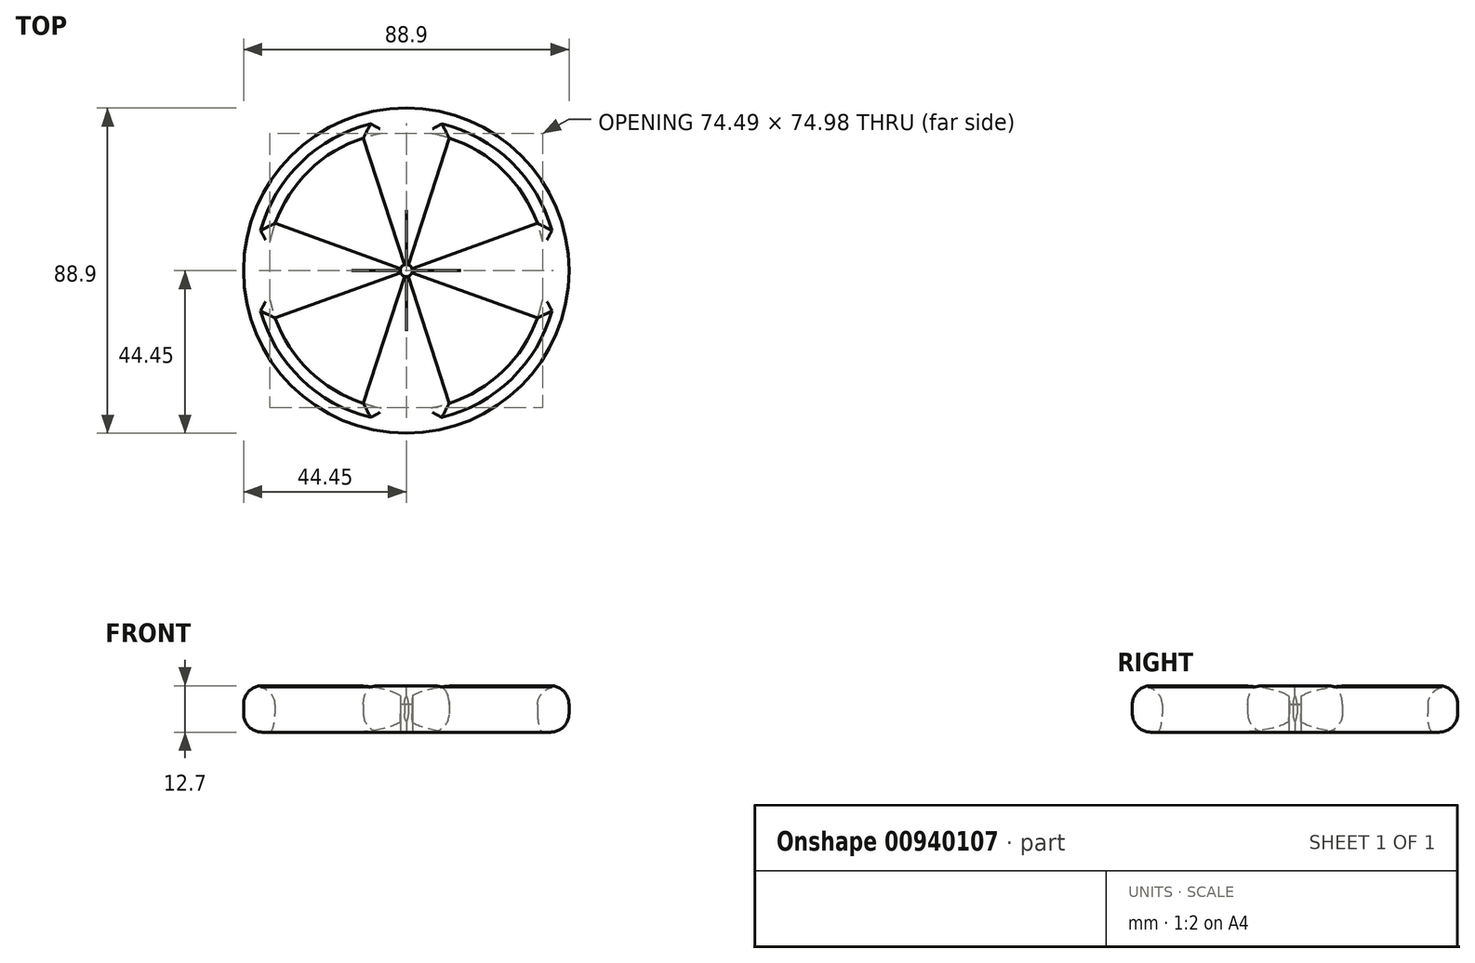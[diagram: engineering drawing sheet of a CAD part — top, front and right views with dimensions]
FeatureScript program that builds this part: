
annotation { "Feature Type Name" : "Feature", "Feature Type Description" : "" }
export const myFeature = defineFeature(function(context is Context, id is Id, definition is map)
    precondition{}
    {
        {
            var Q0;
            Q0=qCreatedBy(makeId("Top.planeOp"),FACE);
            var sketch = newSketch(context, id + "F0", { "sketchPlane" : qUnion([Q0])});
            skCircle(sketch, "E0", {"center": v(0, 0) * mm, "radius": 38.1 * mm});
            skLineSegment(sketch, "E1", {"start": v(0, 0) * mm, "end": v(-38.1, 0) * mm});
            skLineSegment(sketch, "E2", {"start": v(-38.1, 0) * mm, "end": v(38.1, 0) * mm});
            skLineSegment(sketch, "E3", {"start": v(0, 38.1) * mm, "end": v(0, -38.1) * mm});
            skLineSegment(sketch, "E4", {"start": v(0, 0) * mm, "end": v(-35.84, 12.92) * mm});
            skLineSegment(sketch, "E5.MirrorCS", {"start": v(0, 0) * mm, "end": v(35.84, 12.92) * mm});
            skLineSegment(sketch, "E6.MirrorCS", {"start": v(0, 0) * mm, "end": v(-35.84, -12.92) * mm});
            skLineSegment(sketch, "E7.MirrorCS", {"start": v(0, 0) * mm, "end": v(35.84, -12.92) * mm});
            skLineSegment(sketch, "E8", {"start": v(0, 0) * mm, "end": v(11.73, -36.25) * mm});
            skLineSegment(sketch, "E9.MirrorCS", {"start": v(0, 0) * mm, "end": v(-11.73, -36.25) * mm});
            skCircle(sketch, "E10.0", {"center": v(0, 0) * mm, "radius": 44.45 * mm});
            skCircle(sketch, "E11", {"center": v(0, 0) * mm, "radius": 1.66 * mm});
            skLineSegment(sketch, "E12.MirrorCS", {"start": v(0, 0) * mm, "end": v(11.73, 36.25) * mm});
            skLineSegment(sketch, "E13.MirrorCS", {"start": v(0, 0) * mm, "end": v(-11.73, 36.25) * mm});
            skSolve(sketch);
        }
        {
            var Q0;
            Q0=makeQuery(id+"F0.imprint","IMPRINT",FACE,{"disambiguationData":[TD([[makeQuery(id+"F0.imprint","IMPRINT",EDGE,{"derivedFrom":sQuery(id+"F0.wireOp",EDGE,"E10.0")}),1.0]])]});
            var Q1;
            {var subQ0=sQuery(id+"F0.wireOp",EDGE,"E3");var subQ1=sQuery(id+"F0.wireOp",EDGE,"E0");var subQ2=makeQuery(id+"F0.imprint","INTERSECT",VERTEX,{"disambiguationData":[OD(1.0)],"derivedFrom":[subQ1,subQ0]});Q1=makeQuery(id+"F0.imprint","IMPRINT",FACE,{"disambiguationData":[TD([[makeQuery(id+"F0.imprint","IMPRINT",EDGE,{"disambiguationData":[TD([[subQ2,-1.0]])],"derivedFrom":subQ1}),1.0]])]});}
            var Q2;
            {var subQ0=sQuery(id+"F0.wireOp",EDGE,"E9.MirrorCS");var subQ1=sQuery(id+"F0.wireOp",EDGE,"E0");var subQ2=makeQuery(id+"F0.imprint","INTERSECT",VERTEX,{"derivedFrom":[subQ1,subQ0]});Q2=makeQuery(id+"F0.imprint","IMPRINT",FACE,{"disambiguationData":[TD([[makeQuery(id+"F0.imprint","IMPRINT",EDGE,{"disambiguationData":[TD([[subQ2,-1.0]])],"derivedFrom":subQ1}),1.0]])]});}
            var Q3;
            {var subQ0=sQuery(id+"F0.wireOp",EDGE,"E4");var subQ1=sQuery(id+"F0.wireOp",EDGE,"E0");var subQ2=makeQuery(id+"F0.imprint","INTERSECT",VERTEX,{"derivedFrom":[subQ1,subQ0]});Q3=makeQuery(id+"F0.imprint","IMPRINT",FACE,{"disambiguationData":[TD([[makeQuery(id+"F0.imprint","IMPRINT",EDGE,{"disambiguationData":[TD([[subQ2,-1.0]])],"derivedFrom":subQ1}),1.0]])]});}
            var Q4;
            {var subQ0=sQuery(id+"F0.wireOp",EDGE,"E1");var subQ1=sQuery(id+"F0.wireOp",EDGE,"E0");var subQ2=makeQuery(id+"F0.imprint","INTERSECT",VERTEX,{"derivedFrom":[subQ1,subQ0]});Q4=makeQuery(id+"F0.imprint","IMPRINT",FACE,{"disambiguationData":[TD([[makeQuery(id+"F0.imprint","IMPRINT",EDGE,{"disambiguationData":[TD([[subQ2,-1.0]])],"derivedFrom":subQ1}),1.0]])]});}
            var Q5;
            {var subQ0=sQuery(id+"F0.wireOp",EDGE,"E5.MirrorCS");var subQ1=sQuery(id+"F0.wireOp",EDGE,"E0");var subQ2=makeQuery(id+"F0.imprint","INTERSECT",VERTEX,{"derivedFrom":[subQ1,subQ0]});Q5=makeQuery(id+"F0.imprint","IMPRINT",FACE,{"disambiguationData":[TD([[makeQuery(id+"F0.imprint","IMPRINT",EDGE,{"disambiguationData":[TD([[subQ2,1.0]])],"derivedFrom":subQ1}),1.0]])]});}
            var Q6;
            {var subQ0=sQuery(id+"F0.wireOp",EDGE,"E2");var subQ1=sQuery(id+"F0.wireOp",EDGE,"E0");var subQ2=makeQuery(id+"F0.imprint","INTERSECT",VERTEX,{"derivedFrom":[subQ1,subQ0]});Q6=makeQuery(id+"F0.imprint","IMPRINT",FACE,{"disambiguationData":[TD([[makeQuery(id+"F0.imprint","IMPRINT",EDGE,{"disambiguationData":[TD([[subQ2,1.0]])],"derivedFrom":subQ1}),1.0]])]});}
            var Q7;
            {var subQ0=sQuery(id+"F0.wireOp",EDGE,"E3");var subQ1=sQuery(id+"F0.wireOp",EDGE,"E0");var subQ2=makeQuery(id+"F0.imprint","INTERSECT",VERTEX,{"disambiguationData":[OD(0.0)],"derivedFrom":[subQ1,subQ0]});Q7=makeQuery(id+"F0.imprint","IMPRINT",FACE,{"disambiguationData":[TD([[makeQuery(id+"F0.imprint","IMPRINT",EDGE,{"disambiguationData":[TD([[subQ2,-1.0]])],"derivedFrom":subQ1}),1.0]])]});}
            var Q8;
            {var subQ0=sQuery(id+"F0.wireOp",EDGE,"E3");var subQ1=sQuery(id+"F0.wireOp",EDGE,"E0");var subQ2=makeQuery(id+"F0.imprint","INTERSECT",VERTEX,{"disambiguationData":[OD(0.0)],"derivedFrom":[subQ1,subQ0]});Q8=makeQuery(id+"F0.imprint","IMPRINT",FACE,{"disambiguationData":[TD([[makeQuery(id+"F0.imprint","IMPRINT",EDGE,{"disambiguationData":[TD([[subQ2,1.0]])],"derivedFrom":subQ1}),1.0]])]});}
            extrude(context, id + "F1", {"entities" : qUnion([Q0, Q1, Q2, Q3, Q4, Q5, Q6, Q7, Q8]), "depth" : 12.7 * mm, "offsetDistance" : 25.4 * mm});
        }
        {
            var Q0;
            Q0=makeQuery(id+"F1.opExtrude","CAP_EDGE",EDGE,{"disambiguationData":[OSD([sQuery(id+"F0.wireOp",EDGE,"E10.0")])],"isStart":false});
            var Q1;
            Q1=makeQuery(id+"F1.opExtrude","CAP_EDGE",EDGE,{"disambiguationData":[OSD([sQuery(id+"F0.wireOp",EDGE,"E10.0")])],"isStart":true});
            fillet(context, id + "F2", {"entities" : qUnion([Q0, Q1]), "radius" : 5.08 * mm, "tangentPropagation" : true, "allowEdgeOverflow" : false});
        }
        {
            var Q0;
            Q0=makeQuery(id+"F1.opExtrude","CAP_EDGE",EDGE,{"disambiguationData":[OSD([sQuery(id+"F0.wireOp",EDGE,"E6.MirrorCS")])],"isStart":false});
            var Q1;
            Q1=makeQuery(id+"F1.opExtrude","CAP_EDGE",EDGE,{"disambiguationData":[OSD([sQuery(id+"F0.wireOp",EDGE,"E4")])],"isStart":false});
            var Q2;
            Q2=makeQuery(id+"F1.opExtrude","CAP_EDGE",EDGE,{"disambiguationData":[OSD([sQuery(id+"F0.wireOp",EDGE,"E6.MirrorCS")])],"isStart":true});
            var Q3;
            Q3=makeQuery(id+"F1.opExtrude","CAP_EDGE",EDGE,{"disambiguationData":[OSD([sQuery(id+"F0.wireOp",EDGE,"E8")])],"isStart":false});
            var Q4;
            Q4=makeQuery(id+"F1.opExtrude","CAP_EDGE",EDGE,{"disambiguationData":[OSD([sQuery(id+"F0.wireOp",EDGE,"E9.MirrorCS")])],"isStart":false});
            var Q5;
            Q5=makeQuery(id+"F1.opExtrude","CAP_EDGE",EDGE,{"disambiguationData":[OSD([sQuery(id+"F0.wireOp",EDGE,"E7.MirrorCS")])],"isStart":false});
            var Q6;
            Q6=makeQuery(id+"F1.opExtrude","CAP_EDGE",EDGE,{"disambiguationData":[OSD([sQuery(id+"F0.wireOp",EDGE,"E7.MirrorCS")])],"isStart":true});
            var Q7;
            Q7=makeQuery(id+"F1.opExtrude","CAP_EDGE",EDGE,{"disambiguationData":[OSD([sQuery(id+"F0.wireOp",EDGE,"E9.MirrorCS")])],"isStart":true});
            var Q8;
            Q8=makeQuery(id+"F1.opExtrude","CAP_EDGE",EDGE,{"disambiguationData":[OSD([sQuery(id+"F0.wireOp",EDGE,"E8")])],"isStart":true});
            var Q9;
            Q9=makeQuery(id+"F1.opExtrude","CAP_EDGE",EDGE,{"disambiguationData":[OSD([sQuery(id+"F0.wireOp",EDGE,"E5.MirrorCS")])],"isStart":true});
            var Q10;
            Q10=makeQuery(id+"F1.opExtrude","CAP_EDGE",EDGE,{"disambiguationData":[OSD([sQuery(id+"F0.wireOp",EDGE,"E5.MirrorCS")])],"isStart":false});
            var Q11;
            Q11=makeQuery(id+"F1.opExtrude","CAP_EDGE",EDGE,{"disambiguationData":[OSD([sQuery(id+"F0.wireOp",EDGE,"E4")])],"isStart":true});
            fillet(context, id + "F3", {"entities" : qUnion([Q0, Q1, Q2, Q3, Q4, Q5, Q6, Q7, Q8, Q9, Q10, Q11]), "radius" : 5.08 * mm, "tangentPropagation" : true, "allowEdgeOverflow" : false});
        }
        {
            var Q0;
            {var subQ0=sQuery(id+"F0.wireOp",EDGE,"E11");var subQ1=sQuery(id+"F0.wireOp",EDGE,"E1");var subQ2=makeQuery(id+"F0.imprint","INTERSECT",VERTEX,{"derivedFrom":[subQ1,subQ0]});Q0=makeQuery(id+"F0.imprint","IMPRINT",FACE,{"disambiguationData":[TD([[makeQuery(id+"F0.imprint","IMPRINT",EDGE,{"disambiguationData":[TD([[subQ2,-1.0]])],"derivedFrom":subQ0}),1.0]])]});}
            var Q1;
            {var subQ0=sQuery(id+"F0.wireOp",EDGE,"E11");var subQ1=sQuery(id+"F0.wireOp",EDGE,"E1");var subQ2=makeQuery(id+"F0.imprint","INTERSECT",VERTEX,{"derivedFrom":[subQ1,subQ0]});Q1=makeQuery(id+"F0.imprint","IMPRINT",FACE,{"disambiguationData":[TD([[makeQuery(id+"F0.imprint","IMPRINT",EDGE,{"disambiguationData":[TD([[subQ2,1.0]])],"derivedFrom":subQ0}),1.0]])]});}
            var Q2;
            {var subQ0=sQuery(id+"F0.wireOp",EDGE,"E11");var subQ1=sQuery(id+"F0.wireOp",EDGE,"E2");var subQ2=makeQuery(id+"F0.imprint","INTERSECT",VERTEX,{"derivedFrom":[subQ1,subQ0]});Q2=makeQuery(id+"F0.imprint","IMPRINT",FACE,{"disambiguationData":[TD([[makeQuery(id+"F0.imprint","IMPRINT",EDGE,{"disambiguationData":[TD([[subQ2,-1.0]])],"derivedFrom":subQ0}),1.0]])]});}
            var Q3;
            {var subQ0=sQuery(id+"F0.wireOp",EDGE,"E11");var subQ1=sQuery(id+"F0.wireOp",EDGE,"E2");var subQ2=makeQuery(id+"F0.imprint","INTERSECT",VERTEX,{"derivedFrom":[subQ1,subQ0]});Q3=makeQuery(id+"F0.imprint","IMPRINT",FACE,{"disambiguationData":[TD([[makeQuery(id+"F0.imprint","IMPRINT",EDGE,{"disambiguationData":[TD([[subQ2,1.0]])],"derivedFrom":subQ0}),1.0]])]});}
            var Q4;
            {var subQ0=sQuery(id+"F0.wireOp",EDGE,"E8");var subQ3=sQuery(id+"F0.wireOp",EDGE,"E11");var subQ5=makeQuery(id+"F0.imprint","INTERSECT",VERTEX,{"derivedFrom":[subQ0,subQ3]});Q4=makeQuery(id+"F0.imprint","IMPRINT",FACE,{"disambiguationData":[TD([[makeQuery(id+"F0.imprint","IMPRINT",EDGE,{"disambiguationData":[TD([[subQ5,1.0]])],"derivedFrom":subQ3}),1.0]])]});}
            var Q5;
            {var subQ0=sQuery(id+"F0.wireOp",EDGE,"E9.MirrorCS");var subQ3=sQuery(id+"F0.wireOp",EDGE,"E11");var subQ5=makeQuery(id+"F0.imprint","INTERSECT",VERTEX,{"derivedFrom":[subQ0,subQ3]});Q5=makeQuery(id+"F0.imprint","IMPRINT",FACE,{"disambiguationData":[TD([[makeQuery(id+"F0.imprint","IMPRINT",EDGE,{"disambiguationData":[TD([[subQ5,-1.0]])],"derivedFrom":subQ3}),1.0]])]});}
            var Q6;
            {var subQ1=sQuery(id+"F0.wireOp",EDGE,"E6.MirrorCS");var subQ3=sQuery(id+"F0.wireOp",EDGE,"E11");var subQ4=makeQuery(id+"F0.imprint","INTERSECT",VERTEX,{"derivedFrom":[subQ1,subQ3]});Q6=makeQuery(id+"F0.imprint","IMPRINT",FACE,{"disambiguationData":[TD([[makeQuery(id+"F0.imprint","IMPRINT",EDGE,{"disambiguationData":[TD([[subQ4,-1.0]])],"derivedFrom":subQ3}),1.0]])]});}
            var Q7;
            {var subQ1=sQuery(id+"F0.wireOp",EDGE,"E7.MirrorCS");var subQ3=sQuery(id+"F0.wireOp",EDGE,"E11");var subQ4=makeQuery(id+"F0.imprint","INTERSECT",VERTEX,{"derivedFrom":[subQ1,subQ3]});Q7=makeQuery(id+"F0.imprint","IMPRINT",FACE,{"disambiguationData":[TD([[makeQuery(id+"F0.imprint","IMPRINT",EDGE,{"disambiguationData":[TD([[subQ4,1.0]])],"derivedFrom":subQ3}),1.0]])]});}
            var Q8;
            {var subQ0=sQuery(id+"F0.wireOp",EDGE,"E12.MirrorCS");var subQ3=sQuery(id+"F0.wireOp",EDGE,"E11");var subQ5=makeQuery(id+"F0.imprint","INTERSECT",VERTEX,{"derivedFrom":[subQ3,subQ0]});Q8=makeQuery(id+"F0.imprint","IMPRINT",FACE,{"disambiguationData":[TD([[makeQuery(id+"F0.imprint","IMPRINT",EDGE,{"disambiguationData":[TD([[subQ5,-1.0]])],"derivedFrom":subQ3}),1.0]])]});}
            var Q9;
            {var subQ0=sQuery(id+"F0.wireOp",EDGE,"E13.MirrorCS");var subQ3=sQuery(id+"F0.wireOp",EDGE,"E11");var subQ5=makeQuery(id+"F0.imprint","INTERSECT",VERTEX,{"derivedFrom":[subQ3,subQ0]});Q9=makeQuery(id+"F0.imprint","IMPRINT",FACE,{"disambiguationData":[TD([[makeQuery(id+"F0.imprint","IMPRINT",EDGE,{"disambiguationData":[TD([[subQ5,1.0]])],"derivedFrom":subQ3}),1.0]])]});}
            var Q10;
            {var subQ1=sQuery(id+"F0.wireOp",EDGE,"E4");var subQ3=sQuery(id+"F0.wireOp",EDGE,"E11");var subQ4=makeQuery(id+"F0.imprint","INTERSECT",VERTEX,{"derivedFrom":[subQ1,subQ3]});Q10=makeQuery(id+"F0.imprint","IMPRINT",FACE,{"disambiguationData":[TD([[makeQuery(id+"F0.imprint","IMPRINT",EDGE,{"disambiguationData":[TD([[subQ4,1.0]])],"derivedFrom":subQ3}),1.0]])]});}
            var Q11;
            {var subQ1=sQuery(id+"F0.wireOp",EDGE,"E5.MirrorCS");var subQ3=sQuery(id+"F0.wireOp",EDGE,"E11");var subQ4=makeQuery(id+"F0.imprint","INTERSECT",VERTEX,{"derivedFrom":[subQ1,subQ3]});Q11=makeQuery(id+"F0.imprint","IMPRINT",FACE,{"disambiguationData":[TD([[makeQuery(id+"F0.imprint","IMPRINT",EDGE,{"disambiguationData":[TD([[subQ4,-1.0]])],"derivedFrom":subQ3}),1.0]])]});}
            extrude(context, id + "F4", {"entities" : qUnion([Q0, Q1, Q2, Q3, Q4, Q5, Q6, Q7, Q8, Q9, Q10, Q11]), "depth" : 7.62 * mm, "offsetDistance" : 25.4 * mm});
        }
        {
            var Q0;
            Q0=makeQuery(id+"F1.opExtrude","CAP_EDGE",EDGE,{"disambiguationData":[OSD([sQuery(id+"F0.wireOp",EDGE,"E13.MirrorCS")])],"isStart":false});
            var Q1;
            Q1=makeQuery(id+"F1.opExtrude","CAP_FACE",FACE,{"disambiguationData":[OSD([sQuery(id+"F0.wireOp",EDGE,"E0"),sQuery(id+"F0.wireOp",EDGE,"E4"),sQuery(id+"F0.wireOp",EDGE,"E5.MirrorCS"),sQuery(id+"F0.wireOp",EDGE,"E6.MirrorCS"),sQuery(id+"F0.wireOp",EDGE,"E7.MirrorCS"),sQuery(id+"F0.wireOp",EDGE,"E8"),sQuery(id+"F0.wireOp",EDGE,"E9.MirrorCS"),sQuery(id+"F0.wireOp",EDGE,"E10.0"),sQuery(id+"F0.wireOp",EDGE,"E11"),sQuery(id+"F0.wireOp",EDGE,"E12.MirrorCS"),sQuery(id+"F0.wireOp",EDGE,"E13.MirrorCS")])],"isStart":false});
            var Q2;
            Q2=makeQuery(id+"F1.opExtrude","CAP_EDGE",EDGE,{"disambiguationData":[OSD([sQuery(id+"F0.wireOp",EDGE,"E12.MirrorCS")])],"isStart":true});
            var Q3;
            Q3=makeQuery(id+"F1.opExtrude","CAP_EDGE",EDGE,{"disambiguationData":[OSD([sQuery(id+"F0.wireOp",EDGE,"E13.MirrorCS")])],"isStart":true});
            fillet(context, id + "F5", {"entities" : qUnion([Q0, Q1, Q2, Q3]), "radius" : 5.08 * mm, "tangentPropagation" : true, "allowEdgeOverflow" : false});
        }
    });
